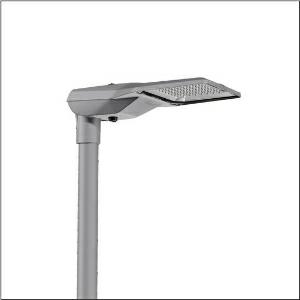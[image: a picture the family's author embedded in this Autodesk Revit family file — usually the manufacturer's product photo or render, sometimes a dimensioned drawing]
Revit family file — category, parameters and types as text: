
# Revit family: streetlight_sl_21_midi___st1_5a_5xe3p43t08mb_72ce
name_source: partatom
category: Lighting Fixtures
units: mm (PartAtom-declared; Revit-internal decimal feet)

## family parameters
Cut with Voids When Loaded = No
Host = Face
Light Source = No
Part Type = Normal
Room Calculation Point = No
Round Connector Dimension = Use Diameter
Shared = No

## types (1)
- --- (1 x LED, 19830 lm, 147 W, 4000K)
    Apparent Load = 147 VA
    CIE Flux Codes = 22 53 95 100 100
    Color Rendering = 70
    Color Temperature = 4000K
    Default Elevation = 1800 mm
    Description = Streetlight SL 21 midi, mast luminaire, primary light control with lens, of PMMA, primary optical cover: cover, of toughened safety glass, transparent, light distribution: ST1.5a, light emission: direct distribution, primary light characteristic: asymmetric, installation type: side-entry, post-top, LED, High Power LED, rated luminous flux: 19.830lm, luminous efficacy: 135lm/W, light colour: 740, colour temperature: 4000K, control gear: D4i, control: overheat protection, constant luminous flux control, time-dependent luminous flux control, flexible luminous flux parameterisation, pre-setting: logarithmic dimming characteristic, mains connection: 230..240V, AC, 50/60Hz, start of lifetime: 147W, end of service life: 155W, reduction: 65W, luminaire housing, of diecast aluminium, powder-coated, SITECO metallic grey (DB 702S), corrosivity category C5 high according to DIN EN ISO 12944, please order mast flange separately, inclination adjustable: 0°, 5°, 10°, 15°, sealing non-destructively replaceable, multi-level sealing system, length: 644mm, width: 335mm, height: 110mm, mast flange for spigot size: 42mm (side-entry): 5XC10008XM4, 60/48mm (side-entry/post-top): 5XC10108XM2, 76/60mm (side-entry/post-top): 5XC10108XM1, mounting height: 4..8m, Smart Interface below and above, protection rating (complete): IP66, insulation class (complete): insulation class II (safety insulation), certification: CE, ENEC, ENEC+, VDE, impact resistance: IK10, permissible operating ambient temperature for outdoor applications: -40..+50°C, standard-compliant lighting for roads and squares, packaging unit: 1 piece

Light Distribution: ST1.5a
    Height = 111 mm
    Lamp = 1 x LED
    Lamp Light Flux = 19830 lm
    Lamp Power = 147 W
    Lamp count = 1
    Length = 644 mm
    Luminous efficacy = 135 lm/W
    Manufacturer = Siteco
    ModVariant = No
    Model = 5XE3P43T08MB
    Number of Poles = 1
    OnlyDefault = Yes
    Power Factor = 1
    Product Name = Streetlight SL 21 midi | ST1.5a
    Product group = mast luminaire | pylon top
    ProductGroupID = 6100
    Protection Class = Protection class II
    Protection Degree = IP 66
    RLX_Detail_Level = 1
    RLX_Emergency_Light_Flux = 0 lm
    RLX_Emergency_Type = 0
    RLX_Emergency_Type_DB = No
    RlxData = <blob elided: 30541 chars, md5=e96cff15>
    Socket = socket
    Standby Power = 0 W
    System Light Flux = 19830 lm
    System Power = 147 W
    Type Comments = factory setting: luminous flux: 100 % | dim-lin: 254 | 750 mA
    Type Image = l_1004304.jpg
    URL = http://relux.com
    VarID = @adj_175545
    Voltage = 0 V
    Weight = 0.00 kg
    Width = 336 mm

## geometry (parser evidence)
native form markers: Blend x4, Sweep x10
no freeform markers — native parametric forms only
